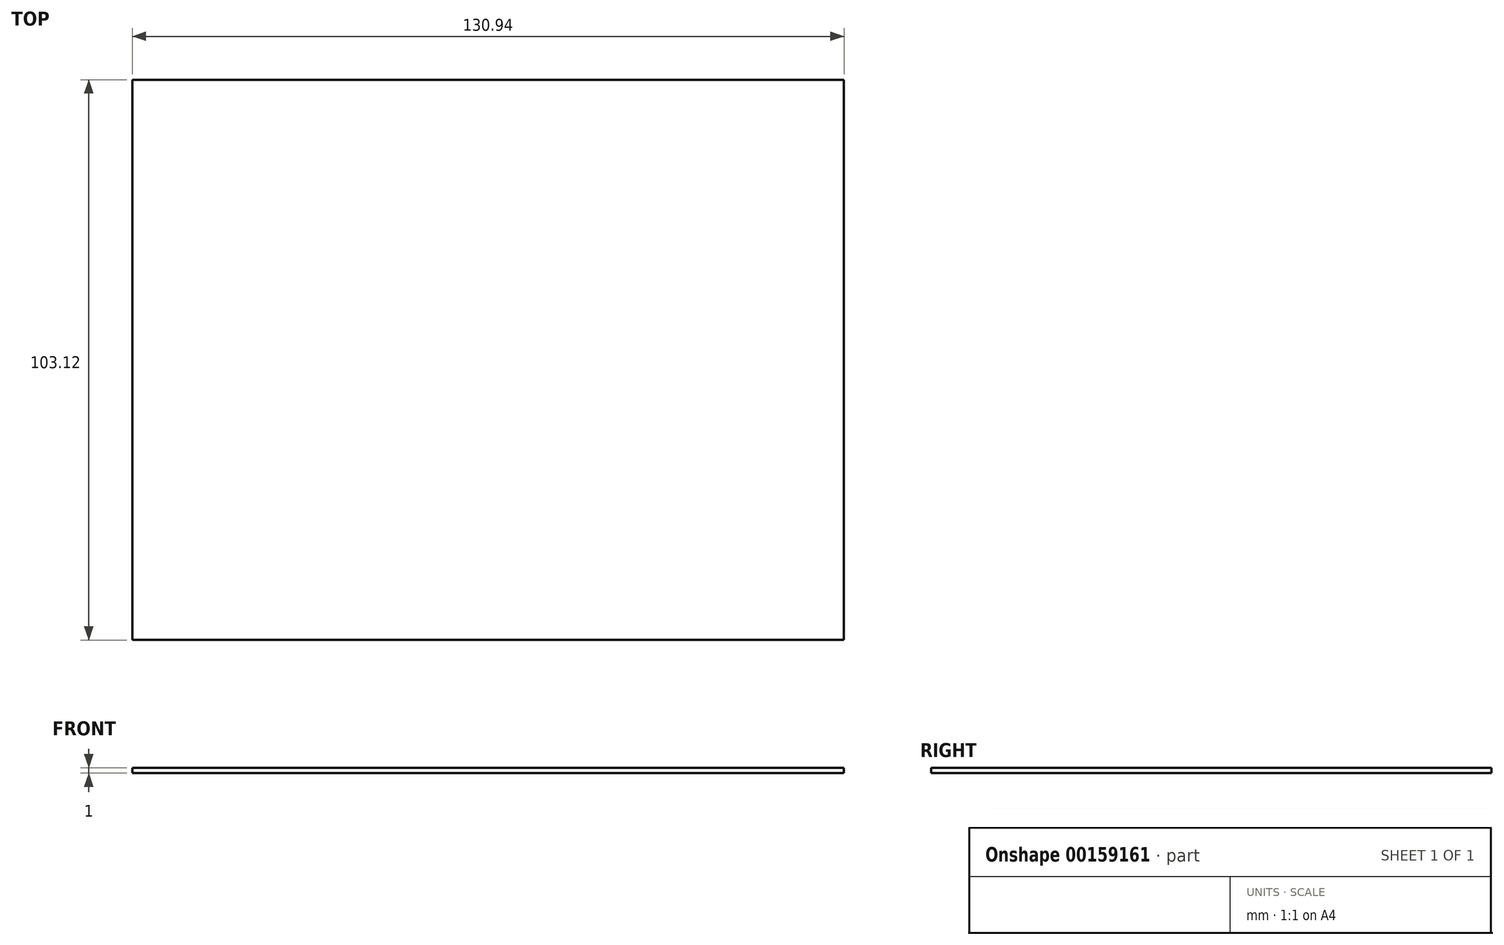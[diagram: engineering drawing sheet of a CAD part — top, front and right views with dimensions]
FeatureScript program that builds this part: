
annotation { "Feature Type Name" : "Feature", "Feature Type Description" : "" }
export const myFeature = defineFeature(function(context is Context, id is Id, definition is map)
    precondition{}
    {
        {
            var Q0;
            Q0=qCreatedBy(makeId("Top.planeOp"),FACE);
            var sketch = newSketch(context, id + "F0", { "sketchPlane" : qUnion([Q0])});
            skLineSegment(sketch, "E0.bottom", {"start": v(65.47, 51.56) * mm, "end": v(-65.47, 51.56) * mm});
            skLineSegment(sketch, "E0.top", {"start": v(65.47, -51.56) * mm, "end": v(-65.47, -51.56) * mm});
            skLineSegment(sketch, "E0.left", {"start": v(65.47, 51.56) * mm, "end": v(65.47, -51.56) * mm});
            skLineSegment(sketch, "E0.right", {"start": v(-65.47, 51.56) * mm, "end": v(-65.47, -51.56) * mm});
            skPoint(sketch, "E0.middle", {"position": v(0, 0) * mm});
            skSolve(sketch);
        }
        {
            var Q0;
            Q0 = qSketchRegion(id + "F0", true);
            extrude(context, id + "F1", {"entities" : qUnion([Q0]), "depth" : 1 * mm});
        }
    });
